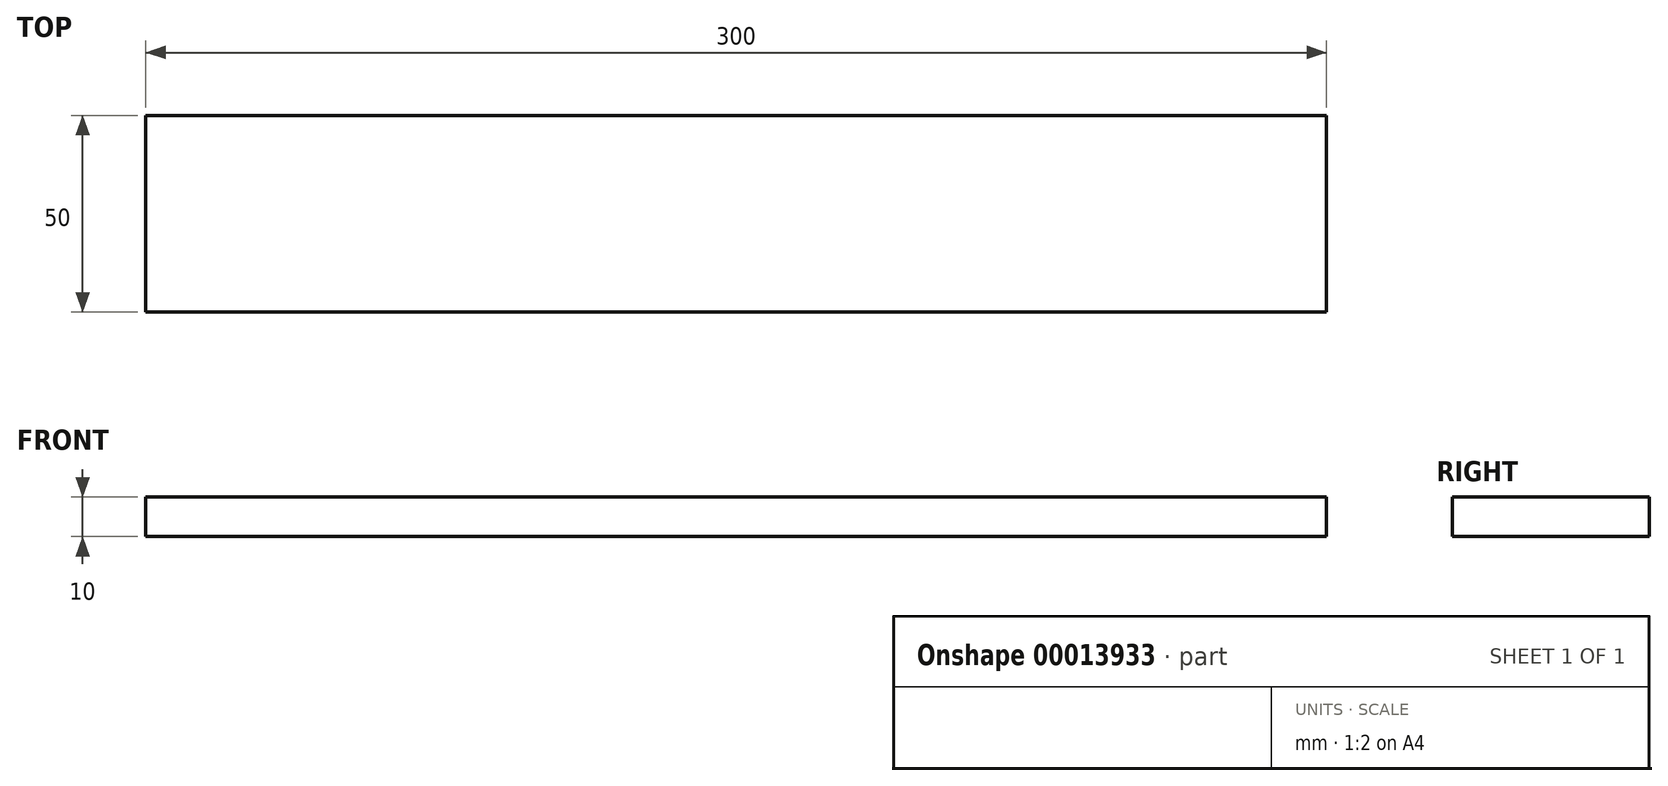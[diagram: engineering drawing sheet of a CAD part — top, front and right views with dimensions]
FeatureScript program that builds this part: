
annotation { "Feature Type Name" : "Feature", "Feature Type Description" : "" }
export const myFeature = defineFeature(function(context is Context, id is Id, definition is map)
    precondition{}
    {
        {
            var Q0;
            Q0=qCreatedBy(makeId("Top.planeOp"),FACE);
            var sketch = newSketch(context, id + "F0", { "sketchPlane" : qUnion([Q0])});
            skLineSegment(sketch, "E0.bottom", {"start": v(-60.03, 16.07) * mm, "end": v(239.97, 16.07) * mm});
            skLineSegment(sketch, "E0.top", {"start": v(-60.03, -33.93) * mm, "end": v(239.97, -33.93) * mm});
            skLineSegment(sketch, "E0.left", {"start": v(-60.03, 16.07) * mm, "end": v(-60.03, -33.93) * mm});
            skLineSegment(sketch, "E0.right", {"start": v(239.97, 16.07) * mm, "end": v(239.97, -33.93) * mm});
            skSolve(sketch);
        }
        {
            var Q0;
            Q0 = qSketchRegion(id + "F0", true);
            extrude(context, id + "F1", {"entities" : qUnion([Q0]), "depth" : 10 * mm});
        }
    });
